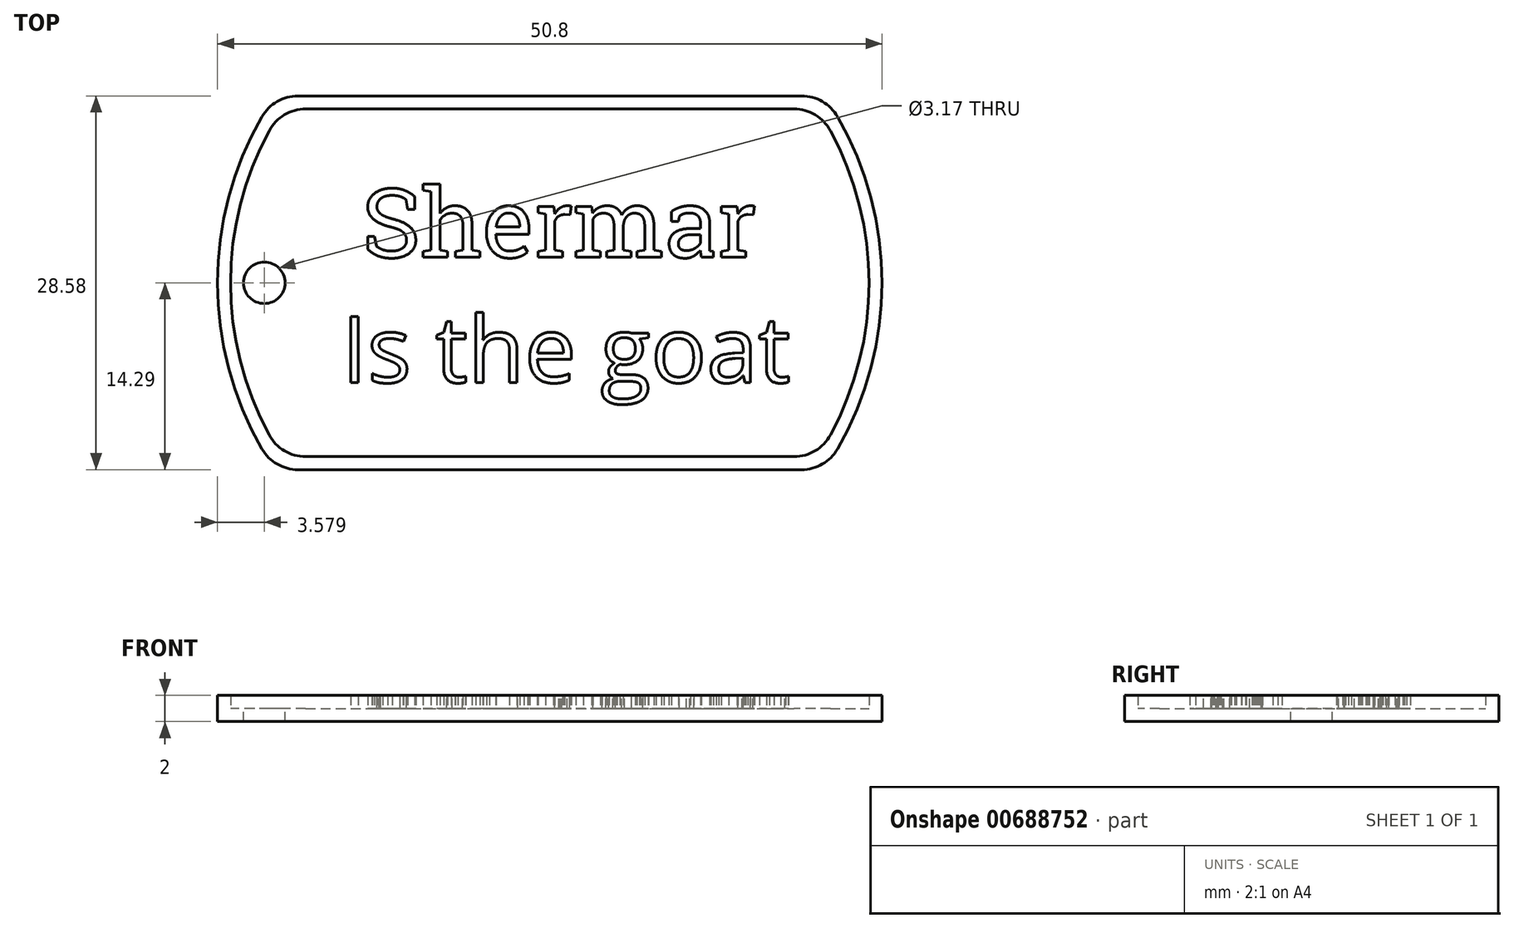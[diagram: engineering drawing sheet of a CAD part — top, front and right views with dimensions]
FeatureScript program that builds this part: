
annotation { "Feature Type Name" : "Feature", "Feature Type Description" : "" }
export const myFeature = defineFeature(function(context is Context, id is Id, definition is map)
    precondition{}
    {
        {
            var Q0;
            Q0=qCreatedBy(makeId("Top.planeOp"),FACE);
            var sketch = newSketch(context, id + "F0", { "sketchPlane" : qUnion([Q0])});
            skArc(sketch, "E0", {"start": v(-22, 12.7) * mm, "mid": v(-25.4, 0) * mm, "end": v(-22, -12.7) * mm});
            skLineSegment(sketch, "E1.top", {"start": v(-19.25, -14.29) * mm, "end": v(19.25, -14.29) * mm});
            skArc(sketch, "E2.trimOffspring", {"start": v(22, -12.7) * mm, "mid": v(25.4, 0) * mm, "end": v(22, 12.7) * mm});
            skLineSegment(sketch, "E3", {"start": v(-19.25, 14.29) * mm, "end": v(19.25, 14.29) * mm});
            skPoint(sketch, "E4.visualSharp", {"position": v(-21, 14.29) * mm});
            skArc(sketch, "E4.filletArc", {"start": v(-19.25, 14.29) * mm, "mid": v(-20.83, 13.86) * mm, "end": v(-22, 12.7) * mm});
            skPoint(sketch, "E5.visualSharp", {"position": v(21, 14.29) * mm});
            skArc(sketch, "E5.filletArc", {"start": v(22, 12.7) * mm, "mid": v(20.83, 13.86) * mm, "end": v(19.25, 14.29) * mm});
            skPoint(sketch, "E6.visualSharp", {"position": v(21, -14.29) * mm});
            skArc(sketch, "E6.filletArc", {"start": v(19.25, -14.29) * mm, "mid": v(20.83, -13.86) * mm, "end": v(22, -12.7) * mm});
            skPoint(sketch, "E7.visualSharp", {"position": v(-21, -14.29) * mm});
            skArc(sketch, "E7.filletArc", {"start": v(-22, -12.7) * mm, "mid": v(-20.83, -13.86) * mm, "end": v(-19.25, -14.29) * mm});
            skSolve(sketch);
        }
        {
            var Q0;
            Q0=makeQuery(id+"F0.imprint","IMPRINT",FACE,{"disambiguationData":[TD([[makeQuery(id+"F0.imprint","IMPRINT",EDGE,{"derivedFrom":sQuery(id+"F0.wireOp",EDGE,"E0")}),1.0]])]});
            extrude(context, id + "F1", {"entities" : qUnion([Q0]), "depth" : 1 * mm, "offsetDistance" : 25.4 * mm});
        }
        {
            var Q0;
            Q0=makeQuery(id+"F1.opExtrude","CAP_FACE",FACE,{"disambiguationData":[OSD([sQuery(id+"F0.wireOp",EDGE,"E0"),sQuery(id+"F0.wireOp",EDGE,"E1.top"),sQuery(id+"F0.wireOp",EDGE,"E2.trimOffspring"),sQuery(id+"F0.wireOp",EDGE,"E3"),sQuery(id+"F0.wireOp",EDGE,"E4.filletArc"),sQuery(id+"F0.wireOp",EDGE,"E5.filletArc"),sQuery(id+"F0.wireOp",EDGE,"E6.filletArc"),sQuery(id+"F0.wireOp",EDGE,"E7.filletArc")])],"isStart":false});
            var sketch = newSketch(context, id + "F2", { "sketchPlane" : qUnion([Q0])});
            skLineSegment(sketch, "E8.0", {"start": v(-18.66, 13.29) * mm, "end": v(18.66, 13.29) * mm});
            skArc(sketch, "E8.1", {"start": v(-21.45, 11.63) * mm, "mid": v(-24.4, 0) * mm, "end": v(-21.45, -11.63) * mm});
            skLineSegment(sketch, "E8.2", {"start": v(-18.66, -13.29) * mm, "end": v(18.66, -13.29) * mm});
            skArc(sketch, "E8.3", {"start": v(21.45, -11.63) * mm, "mid": v(24.4, 0) * mm, "end": v(21.45, 11.63) * mm});
            skPoint(sketch, "E9.visualSharp", {"position": v(-20.46, 13.29) * mm});
            skArc(sketch, "E9.filletArc", {"start": v(-18.66, 13.29) * mm, "mid": v(-20.29, 12.84) * mm, "end": v(-21.45, 11.63) * mm});
            skPoint(sketch, "E10.visualSharp", {"position": v(20.46, 13.29) * mm});
            skArc(sketch, "E10.filletArc", {"start": v(21.45, 11.63) * mm, "mid": v(20.29, 12.84) * mm, "end": v(18.66, 13.29) * mm});
            skPoint(sketch, "E11.visualSharp", {"position": v(20.46, -13.29) * mm});
            skArc(sketch, "E11.filletArc", {"start": v(18.66, -13.29) * mm, "mid": v(20.29, -12.84) * mm, "end": v(21.45, -11.63) * mm});
            skPoint(sketch, "E12.visualSharp", {"position": v(-20.46, -13.29) * mm});
            skArc(sketch, "E12.filletArc", {"start": v(-21.45, -11.63) * mm, "mid": v(-20.29, -12.84) * mm, "end": v(-18.66, -13.29) * mm});
            skLineSegment(sketch, "E13.0", {"start": v(-19.25, 14.29) * mm, "end": v(19.25, 14.29) * mm});
            skArc(sketch, "E13.1", {"start": v(-22, 12.7) * mm, "mid": v(-25.4, 0) * mm, "end": v(-22, -12.7) * mm});
            skLineSegment(sketch, "E13.2", {"start": v(-19.25, -14.29) * mm, "end": v(19.25, -14.29) * mm});
            skArc(sketch, "E13.3", {"start": v(22, -12.7) * mm, "mid": v(25.4, 0) * mm, "end": v(22, 12.7) * mm});
            skPoint(sketch, "E14.visualSharp", {"position": v(-21, -14.29) * mm});
            skArc(sketch, "E14.filletArc", {"start": v(-22, -12.7) * mm, "mid": v(-20.83, -13.86) * mm, "end": v(-19.25, -14.29) * mm});
            skPoint(sketch, "E15.visualSharp", {"position": v(21, -14.29) * mm});
            skArc(sketch, "E15.filletArc", {"start": v(19.25, -14.29) * mm, "mid": v(20.83, -13.86) * mm, "end": v(22, -12.7) * mm});
            skPoint(sketch, "E16.visualSharp", {"position": v(21, 14.29) * mm});
            skArc(sketch, "E16.filletArc", {"start": v(22, 12.7) * mm, "mid": v(20.83, 13.86) * mm, "end": v(19.25, 14.29) * mm});
            skPoint(sketch, "E17.visualSharp", {"position": v(-21, 14.29) * mm});
            skArc(sketch, "E17.filletArc", {"start": v(-19.25, 14.29) * mm, "mid": v(-20.83, 13.86) * mm, "end": v(-22, 12.7) * mm});
            skSolve(sketch);
        }
        {
            var Q0;
            Q0=makeQuery(id+"F2.imprint","IMPRINT",FACE,{"disambiguationData":[TD([[makeQuery(id+"F2.imprint","IMPRINT",EDGE,{"derivedFrom":sQuery(id+"F2.wireOp",EDGE,"E8.0")}),1.0]])]});
            extrude(context, id + "F3", {"entities" : qUnion([Q0]), "operationType" : NewBodyOperationType.ADD, "depth" : 1 * mm, "offsetDistance" : 25.4 * mm});
        }
        {
            var Q0;
            Q0=makeQuery(id+"F1.opExtrude","CAP_FACE",FACE,{"disambiguationData":[OSD([sQuery(id+"F0.wireOp",EDGE,"E0"),sQuery(id+"F0.wireOp",EDGE,"E1.top"),sQuery(id+"F0.wireOp",EDGE,"E2.trimOffspring"),sQuery(id+"F0.wireOp",EDGE,"E3"),sQuery(id+"F0.wireOp",EDGE,"E4.filletArc"),sQuery(id+"F0.wireOp",EDGE,"E5.filletArc"),sQuery(id+"F0.wireOp",EDGE,"E6.filletArc"),sQuery(id+"F0.wireOp",EDGE,"E7.filletArc")])],"isStart":false});
            var sketch = newSketch(context, id + "F4", { "sketchPlane" : qUnion([Q0])});
            skCircle(sketch, "E18", {"center": v(-21.82, 0) * mm, "radius": 1.59 * mm});
            skSolve(sketch);
        }
        {
            var Q0;
            Q0=makeQuery(id+"F4.imprint","IMPRINT",FACE,{"disambiguationData":[TD([[makeQuery(id+"F4.imprint","IMPRINT",EDGE,{"derivedFrom":sQuery(id+"F4.wireOp",EDGE,"E18")}),1.0]])]});
            extrude(context, id + "F5", {"entities" : qUnion([Q0]), "operationType" : NewBodyOperationType.REMOVE, "oppositeDirection" : true, "depth" : 1 * mm, "offsetDistance" : 25.4 * mm});
        }
        {
            var Q0;
            Q0=makeQuery(id+"F1.opExtrude","CAP_FACE",FACE,{"disambiguationData":[OSD([sQuery(id+"F0.wireOp",EDGE,"E0"),sQuery(id+"F0.wireOp",EDGE,"E1.top"),sQuery(id+"F0.wireOp",EDGE,"E2.trimOffspring"),sQuery(id+"F0.wireOp",EDGE,"E3"),sQuery(id+"F0.wireOp",EDGE,"E4.filletArc"),sQuery(id+"F0.wireOp",EDGE,"E5.filletArc"),sQuery(id+"F0.wireOp",EDGE,"E6.filletArc"),sQuery(id+"F0.wireOp",EDGE,"E7.filletArc")])],"isStart":false});
            var sketch = newSketch(context, id + "F6", { "sketchPlane" : qUnion([Q0])});
            skText(sketch, "E19", { "text": "Shermar", "fontName": "RobotoSlab-Regular.ttf"});
            skText(sketch, "E20", { "text": "Is the goat\n", "fontName": "OpenSans-Regular.ttf"});
            const initialGuessF6  = {"E19": [-0.01436, 0.00195, 1, 0, 0.00528], "E20": [-0.01592, -0.00762, 1, 0, 0.00508]};
            skSetInitialGuess(sketch, initialGuessF6);
            skSolve(sketch);
        }
        {
            var Q0;
            Q0 = qSketchRegion(id + "F6", true);
            extrude(context, id + "F7", {"entities" : qUnion([Q0]), "operationType" : NewBodyOperationType.ADD, "depth" : 1 * mm, "offsetDistance" : 25.4 * mm});
        }
    });
